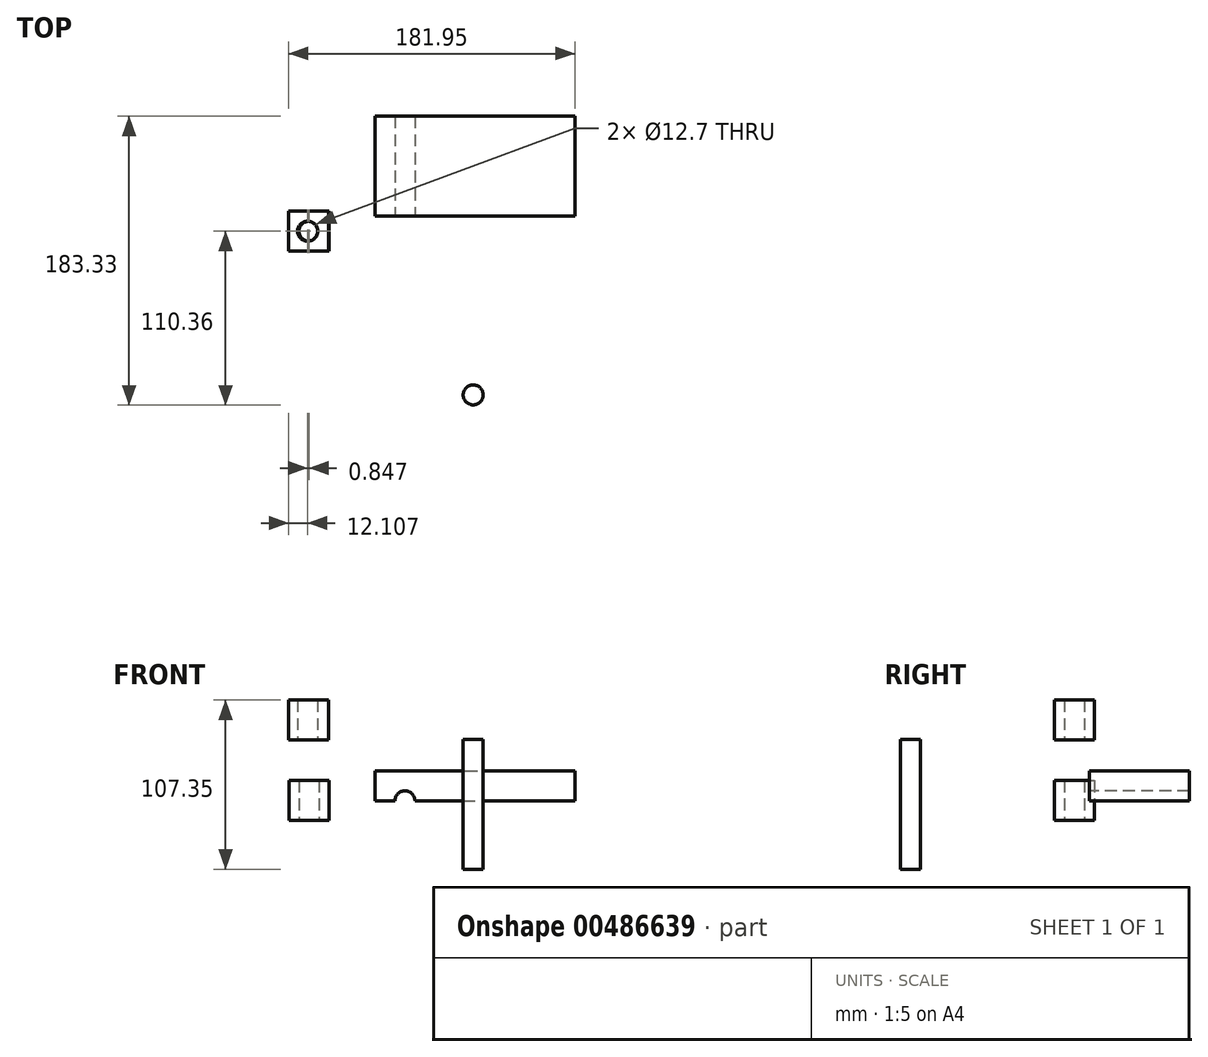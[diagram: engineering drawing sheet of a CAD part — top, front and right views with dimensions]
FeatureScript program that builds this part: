
annotation { "Feature Type Name" : "Feature", "Feature Type Description" : "" }
export const myFeature = defineFeature(function(context is Context, id is Id, definition is map)
    precondition{}
    {
        {
            var Q0;
            Q0=qCreatedBy(makeId("Top.planeOp"),FACE);
            var sketch = newSketch(context, id + "F0", { "sketchPlane" : qUnion([Q0])});
            skCircle(sketch, "E0", {"center": v(43.34, -116.7) * mm, "radius": 6.35 * mm});
            skSolve(sketch);
        }
        {
            var Q0;
            Q0=qCreatedBy(makeId("Top.planeOp"),FACE);
            var sketch = newSketch(context, id + "F1", { "sketchPlane" : qUnion([Q0])});
            skLineSegment(sketch, "E1.bottom", {"start": v(-19, 60.27) * mm, "end": v(108, 60.27) * mm});
            skLineSegment(sketch, "E1.top", {"start": v(-19, -3.23) * mm, "end": v(108, -3.23) * mm});
            skLineSegment(sketch, "E1.left", {"start": v(-19, 60.27) * mm, "end": v(-19, -3.23) * mm});
            skLineSegment(sketch, "E1.right", {"start": v(108, 60.27) * mm, "end": v(108, -3.23) * mm});
            skSolve(sketch);
        }
        {
            var Q0;
            Q0=makeQuery(id+"F1.imprint","IMPRINT",FACE,{"disambiguationData":[TD([[makeQuery(id+"F1.imprint","IMPRINT",EDGE,{"derivedFrom":sQuery(id+"F1.wireOp",EDGE,"E1.bottom")}),-1.0]])]});
            extrude(context, id + "F2", {"entities" : qUnion([Q0]), "depth" : 19.05 * mm});
        }
        {
            var Q0;
            Q0=makeQuery(id+"F2.opExtrude","SWEPT_FACE",FACE,{"disambiguationData":[OSD([sQuery(id+"F1.wireOp",EDGE,"E1.top")])]});
            var sketch = newSketch(context, id + "F3", { "sketchPlane" : qUnion([Q0])});
            skCircle(sketch, "E2", {"center": v(0, 0) * mm, "radius": 6.35 * mm});
            skSolve(sketch);
        }
        {
            var Q0;
            Q0 = qSketchRegion(id + "F3", true);
            extrude(context, id + "F4", {"entities" : qUnion([Q0]), "operationType" : NewBodyOperationType.REMOVE, "oppositeDirection" : true, "depth" : 88.4 * mm});
        }
        {
            var Q0;
            Q0=makeQuery(id+"F0.imprint","IMPRINT",FACE,{"disambiguationData":[TD([[makeQuery(id+"F0.imprint","IMPRINT",EDGE,{"derivedFrom":sQuery(id+"F0.wireOp",EDGE,"E0")}),1.0]])]});
            extrude(context, id + "F5", {"entities" : qUnion([Q0]), "depth" : 39.12 * mm, "offsetDistance" : 25.4 * mm});
        }
        {
            var Q0;
            Q0=makeQuery(id+"F5.opExtrude","CAP_FACE",FACE,{"disambiguationData":[OSD([sQuery(id+"F0.wireOp",EDGE,"E0")])],"isStart":true});
            extrude(context, id + "F6", {"entities" : qUnion([Q0]), "operationType" : NewBodyOperationType.ADD, "depth" : 43.43 * mm, "offsetDistance" : 25.4 * mm});
        }
        {
            var Q0;
            Q0=qCreatedBy(makeId("Front.planeOp"),FACE);
            var sketch = newSketch(context, id + "F7", { "sketchPlane" : qUnion([Q0])});
            skLineSegment(sketch, "E3.bottom", {"start": v(-73.95, 63.92) * mm, "end": v(-48.55, 63.92) * mm});
            skLineSegment(sketch, "E3.top", {"start": v(-73.95, 38.52) * mm, "end": v(-48.55, 38.52) * mm});
            skLineSegment(sketch, "E3.left", {"start": v(-73.95, 63.92) * mm, "end": v(-73.95, 38.52) * mm});
            skLineSegment(sketch, "E3.right", {"start": v(-48.55, 63.92) * mm, "end": v(-48.55, 38.52) * mm});
            skLineSegment(sketch, "E4.bottom", {"start": v(-73.7, 12.87) * mm, "end": v(-48.3, 12.87) * mm});
            skLineSegment(sketch, "E4.top", {"start": v(-73.7, -12.53) * mm, "end": v(-48.3, -12.53) * mm});
            skLineSegment(sketch, "E4.left", {"start": v(-73.7, 12.87) * mm, "end": v(-73.7, -12.53) * mm});
            skLineSegment(sketch, "E4.right", {"start": v(-48.3, 12.87) * mm, "end": v(-48.3, -12.53) * mm});
            skSolve(sketch);
        }
        {
            var Q0;
            Q0=makeQuery(id+"F7.imprint","IMPRINT",FACE,{"disambiguationData":[TD([[makeQuery(id+"F7.imprint","IMPRINT",EDGE,{"derivedFrom":sQuery(id+"F7.wireOp",EDGE,"E3.bottom")}),-1.0]])]});
            var Q1;
            Q1=makeQuery(id+"F7.imprint","IMPRINT",FACE,{"disambiguationData":[TD([[makeQuery(id+"F7.imprint","IMPRINT",EDGE,{"derivedFrom":sQuery(id+"F7.wireOp",EDGE,"tsnVlUzw-rl0Z-wKem-REtV-Lw7vYhlWWXih.bottom")}),-1.0]])]});
            extrude(context, id + "F8", {"entities" : qUnion([Q0, Q1]), "depth" : 25.4 * mm, "offsetDistance" : 25.4 * mm});
        }
        {
            var Q0;
            Q0=makeQuery(id+"F8.opExtrude","SWEPT_FACE",FACE,{"disambiguationData":[OSD([sQuery(id+"F7.wireOp",EDGE,"E3.top")])]});
            var sketch = newSketch(context, id + "F9", { "sketchPlane" : qUnion([Q0])});
            skCircle(sketch, "E5", {"center": v(-61.84, 12.7) * mm, "radius": 6.35 * mm});
            skPoint(sketch, "E5.centerSnap0", {"position": v(-73.95, 12.7) * mm});
            skSolve(sketch);
        }
        {
            var Q0;
            Q0=makeQuery(id+"F7.imprint","IMPRINT",FACE,{"disambiguationData":[TD([[makeQuery(id+"F7.imprint","IMPRINT",EDGE,{"derivedFrom":sQuery(id+"F7.wireOp",EDGE,"E4.bottom")}),-1.0]])]});
            extrude(context, id + "F10", {"entities" : qUnion([Q0]), "depth" : 25.4 * mm, "offsetDistance" : 25.4 * mm});
        }
        {
            var Q0;
            Q0=makeQuery(id+"F10.opExtrude","SWEPT_FACE",FACE,{"disambiguationData":[OSD([sQuery(id+"F7.wireOp",EDGE,"E4.top")])]});
            var sketch = newSketch(context, id + "F11", { "sketchPlane" : qUnion([Q0])});
            skCircle(sketch, "E6", {"center": v(-61, 12.7) * mm, "radius": 6.35 * mm});
            skPoint(sketch, "E6.centerSnap0", {"position": v(-61, 0) * mm});
            skPoint(sketch, "E6.centerSnap1", {"position": v(-73.7, 12.7) * mm});
            skSolve(sketch);
        }
        {
            var Q0;
            Q0=makeQuery(id+"F11.imprint","IMPRINT",FACE,{"disambiguationData":[TD([[makeQuery(id+"F11.imprint","IMPRINT",EDGE,{"derivedFrom":sQuery(id+"F11.wireOp",EDGE,"E6")}),1.0]])]});
            extrude(context, id + "F12", {"entities" : qUnion([Q0]), "operationType" : NewBodyOperationType.REMOVE, "oppositeDirection" : true, "depth" : 47.24 * mm, "offsetDistance" : 25.4 * mm});
        }
        {
            var Q0;
            Q0=makeQuery(id+"F9.imprint","IMPRINT",FACE,{"disambiguationData":[TD([[makeQuery(id+"F9.imprint","IMPRINT",EDGE,{"derivedFrom":sQuery(id+"F9.wireOp",EDGE,"E5")}),1.0]])]});
            extrude(context, id + "F13", {"entities" : qUnion([Q0]), "operationType" : NewBodyOperationType.REMOVE, "oppositeDirection" : true, "depth" : 47 * mm, "offsetDistance" : 25.4 * mm});
        }
    });
